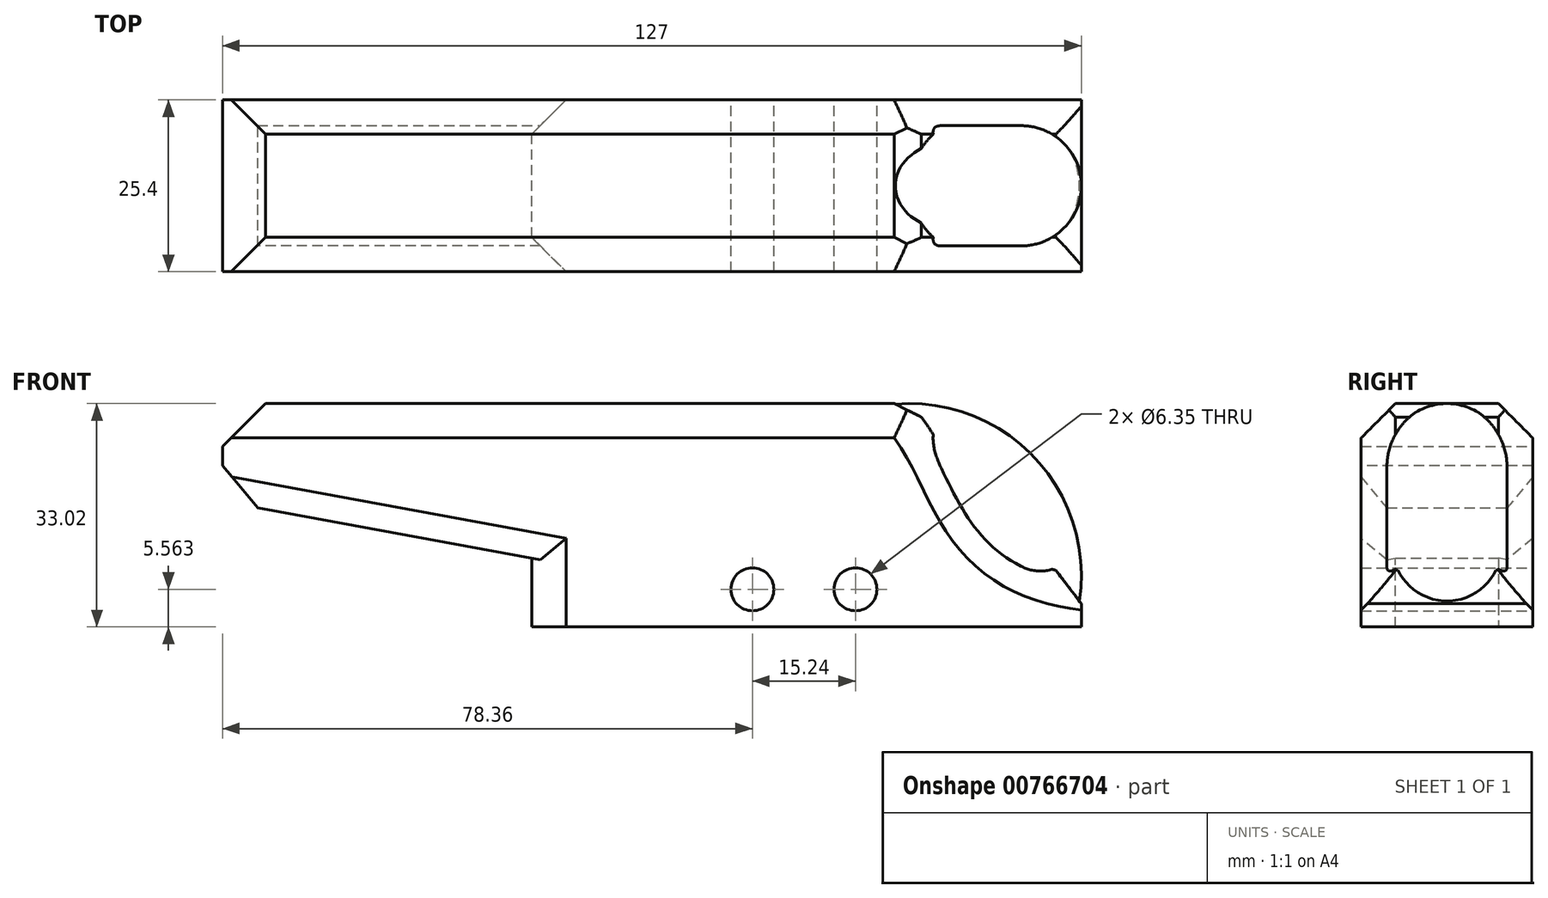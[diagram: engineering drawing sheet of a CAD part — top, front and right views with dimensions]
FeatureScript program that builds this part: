
annotation { "Feature Type Name" : "Feature", "Feature Type Description" : "" }
export const myFeature = defineFeature(function(context is Context, id is Id, definition is map)
    precondition{}
    {
        {
            var Q0;
            Q0=qCreatedBy(makeId("Front.planeOp"),FACE);
            var sketch = newSketch(context, id + "F0", { "sketchPlane" : qUnion([Q0])});
            skLineSegment(sketch, "E0", {"start": v(-66.77, 17.2) * mm, "end": v(34.83, 17.2) * mm});
            skLineSegment(sketch, "E1", {"start": v(60.23, -8.2) * mm, "end": v(60.23, -15.81) * mm});
            skLineSegment(sketch, "E2", {"start": v(60.23, -15.81) * mm, "end": v(-21.05, -15.81) * mm});
            skLineSegment(sketch, "E3", {"start": v(-21.05, -15.81) * mm, "end": v(-21.05, -5.65) * mm});
            skLineSegment(sketch, "E4", {"start": v(-21.05, -5.65) * mm, "end": v(-66.77, 2.75) * mm});
            skLineSegment(sketch, "E5", {"start": v(-66.77, 17.2) * mm, "end": v(-66.77, 2.75) * mm});
            skPoint(sketch, "E6.visualSharp", {"position": v(60.23, 17.2) * mm});
            skArc(sketch, "E6.filletArc", {"start": v(60.23, -8.2) * mm, "mid": v(52.79, 9.77) * mm, "end": v(34.83, 17.2) * mm});
            skCircle(sketch, "E7", {"center": v(11.59, -10.25) * mm, "radius": 3.18 * mm});
            skCircle(sketch, "E8", {"center": v(26.83, -10.25) * mm, "radius": 3.18 * mm});
            skFitSpline(sketch, "E9", {"points": [v(34.83, 17.2) * mm, v(60.23, -8.2) * mm], "startDerivative": vector(25.4, -25.4) * mm, "endDerivative": vector(55.94, -7.95) * mm});
            skSolve(sketch);
        }
        {
            var Q0;
            Q0=makeQuery(id+"F0.imprint","IMPRINT",FACE,{"disambiguationData":[TD([[makeQuery(id+"F0.imprint","IMPRINT",EDGE,{"derivedFrom":sQuery(id+"F0.wireOp",EDGE,"E0")}),-1.0]])]});
            extrude(context, id + "F1", {"entities" : qUnion([Q0]), "depth" : 12.7 * mm, "offsetDistance" : 25.4 * mm});
        }
        {
            var Q0;
            Q0=makeQuery(id+"F0.imprint","IMPRINT",FACE,{"disambiguationData":[TD([[makeQuery(id+"F0.imprint","IMPRINT",EDGE,{"derivedFrom":sQuery(id+"F0.wireOp",EDGE,"E0")}),-1.0]])]});
            extrude(context, id + "F2", {"entities" : qUnion([Q0]), "operationType" : NewBodyOperationType.ADD, "depth" : -12.7 * mm, "offsetDistance" : 25.4 * mm});
        }
        {
            var Q0;
            Q0=makeQuery(id+"F0.imprint","IMPRINT",FACE,{"disambiguationData":[TD([[makeQuery(id+"F0.imprint","IMPRINT",EDGE,{"derivedFrom":sQuery(id+"F0.wireOp",EDGE,"E6.filletArc")}),1.0]])]});
            extrude(context, id + "F3", {"entities" : qUnion([Q0]), "operationType" : NewBodyOperationType.ADD, "depth" : 8.9 * mm, "offsetDistance" : 25.4 * mm});
        }
        {
            var Q0;
            Q0=makeQuery(id+"F0.imprint","IMPRINT",FACE,{"disambiguationData":[TD([[makeQuery(id+"F0.imprint","IMPRINT",EDGE,{"derivedFrom":sQuery(id+"F0.wireOp",EDGE,"E6.filletArc")}),1.0]])]});
            extrude(context, id + "F4", {"entities" : qUnion([Q0]), "operationType" : NewBodyOperationType.ADD, "depth" : -8.9 * mm, "offsetDistance" : 25.4 * mm});
        }
        {
            var Q0;
            Q0=makeQuery(id+"F4.opExtrude","CAP_EDGE",EDGE,{"disambiguationData":[OSD([sQuery(id+"F0.wireOp",EDGE,"E6.filletArc")])],"isStart":false});
            var Q1;
            Q1=makeQuery(id+"F3.opExtrude","CAP_EDGE",EDGE,{"disambiguationData":[OSD([sQuery(id+"F0.wireOp",EDGE,"E6.filletArc")])],"isStart":false});
            fillet(context, id + "F5", {"entities" : qUnion([Q0, Q1]), "radius" : 8.9 * mm, "tangentPropagation" : true, "allowEdgeOverflow" : false});
        }
        {
            var Q0;
            Q0=makeQuery(id+"F2.opExtrude","CAP_EDGE",EDGE,{"disambiguationData":[OSD([sQuery(id+"F0.wireOp",EDGE,"E9")])],"isStart":false});
            var Q1;
            Q1=makeQuery(id+"F1.opExtrude","CAP_EDGE",EDGE,{"disambiguationData":[OSD([sQuery(id+"F0.wireOp",EDGE,"E9")])],"isStart":false});
            var Q2;
            {var subQ0=sQuery(id+"F0.wireOp",EDGE,"E0");var subQ1=sQuery(id+"F0.wireOp",EDGE,"E9");var subQ2=sQuery(id+"F0.wireOp",EDGE,"E6.filletArc");Q2=makeQuery(id+"F3.boolean.opBoolean","SPLIT",EDGE,{"disambiguationData":[TD([makeQuery(id+"F3.opExtrude","CAP_FACE",FACE,{"disambiguationData":[OSD([subQ2,subQ1])],"isStart":false})])],"derivedFrom":makeQuery(id+"F2.boolean.opBoolean","MERGE",EDGE,{"derivedFrom":[makeQuery(id+"F1.opExtrude","SWEPT_EDGE",EDGE,{"disambiguationData":[OSD([subQ0,subQ2,subQ1])]}),makeQuery(id+"F2.opExtrude","SWEPT_EDGE",EDGE,{"disambiguationData":[OSD([subQ0,subQ2,subQ1])]})]})});}
            var Q3;
            {var subQ0=sQuery(id+"F0.wireOp",EDGE,"E1");var subQ1=sQuery(id+"F0.wireOp",EDGE,"E9");var subQ2=sQuery(id+"F0.wireOp",EDGE,"E6.filletArc");Q3=makeQuery(id+"F4.boolean.opBoolean","SPLIT",EDGE,{"derivedFrom":makeQuery(id+"F3.boolean.opBoolean","SPLIT",EDGE,{"disambiguationData":[TD([makeQuery(id+"F3.opExtrude","CAP_FACE",FACE,{"disambiguationData":[OSD([subQ2,subQ1])],"isStart":true})])],"derivedFrom":makeQuery(id+"F2.boolean.opBoolean","MERGE",EDGE,{"derivedFrom":[makeQuery(id+"F1.opExtrude","SWEPT_EDGE",EDGE,{"disambiguationData":[OSD([subQ0,subQ2,subQ1])]}),makeQuery(id+"F2.opExtrude","SWEPT_EDGE",EDGE,{"disambiguationData":[OSD([subQ0,subQ2,subQ1])]})]})})});}
            chamfer(context, id + "F6", {"entities" : qUnion([Q0, Q1, Q2, Q3]), "width" : 5.08 * mm, "tangentPropagation" : true});
        }
        {
            var Q0;
            Q0=makeQuery(id+"F2.opExtrude","CAP_EDGE",EDGE,{"disambiguationData":[OSD([sQuery(id+"F0.wireOp",EDGE,"E0")])],"isStart":false});
            var Q1;
            Q1=makeQuery(id+"F1.opExtrude","CAP_EDGE",EDGE,{"disambiguationData":[OSD([sQuery(id+"F0.wireOp",EDGE,"E0")])],"isStart":false});
            chamfer(context, id + "F7", {"entities" : qUnion([Q0, Q1]), "width" : 5.08 * mm, "tangentPropagation" : true});
        }
        {
            var Q0;
            {var subQ0=sQuery(id+"F0.wireOp",EDGE,"E5");var subQ1=sQuery(id+"F0.wireOp",EDGE,"E4");Q0=makeQuery(id+"F2.boolean.opBoolean","MERGE",EDGE,{"derivedFrom":[makeQuery(id+"F1.opExtrude","SWEPT_EDGE",EDGE,{"disambiguationData":[OSD([subQ1,subQ0])]}),makeQuery(id+"F2.opExtrude","SWEPT_EDGE",EDGE,{"disambiguationData":[OSD([subQ1,subQ0])]})]});}
            var Q1;
            {var subQ0=sQuery(id+"F0.wireOp",EDGE,"E5");var subQ1=sQuery(id+"F0.wireOp",EDGE,"E0");Q1=makeQuery(id+"F2.boolean.opBoolean","MERGE",EDGE,{"derivedFrom":[makeQuery(id+"F1.opExtrude","SWEPT_EDGE",EDGE,{"disambiguationData":[OSD([subQ1,subQ0])]}),makeQuery(id+"F2.opExtrude","SWEPT_EDGE",EDGE,{"disambiguationData":[OSD([subQ1,subQ0])]})]});}
            chamfer(context, id + "F8", {"entities" : qUnion([Q0, Q1]), "width" : 6.35 * mm, "tangentPropagation" : true});
        }
        {
            var Q0;
            Q0=makeQuery(id+"F2.opExtrude","CAP_EDGE",EDGE,{"disambiguationData":[OSD([sQuery(id+"F0.wireOp",EDGE,"E4")])],"isStart":false});
            var Q1;
            Q1=makeQuery(id+"F1.opExtrude","CAP_EDGE",EDGE,{"disambiguationData":[OSD([sQuery(id+"F0.wireOp",EDGE,"E4")])],"isStart":false});
            chamfer(context, id + "F9", {"entities" : qUnion([Q0, Q1]), "width" : 3.8 * mm, "tangentPropagation" : true});
        }
        {
            var Q0;
            Q0=makeQuery(id+"F1.opExtrude","CAP_EDGE",EDGE,{"disambiguationData":[OSD([sQuery(id+"F0.wireOp",EDGE,"E3")])],"isStart":false});
            var Q1;
            Q1=makeQuery(id+"F2.opExtrude","CAP_EDGE",EDGE,{"disambiguationData":[OSD([sQuery(id+"F0.wireOp",EDGE,"E3")])],"isStart":false});
            chamfer(context, id + "F10", {"entities" : qUnion([Q0, Q1]), "width" : 5.08 * mm, "tangentPropagation" : true});
        }
    });
